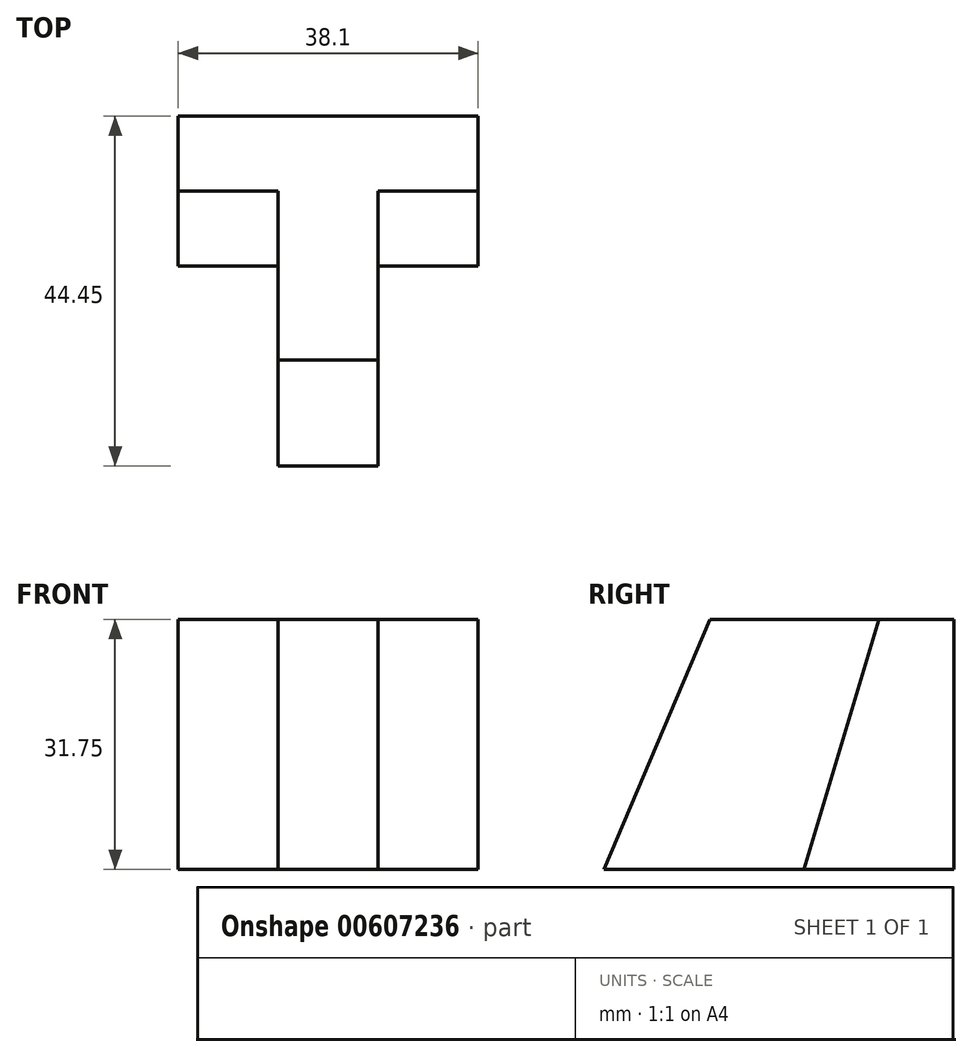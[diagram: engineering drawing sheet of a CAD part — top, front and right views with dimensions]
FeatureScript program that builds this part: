
annotation { "Feature Type Name" : "Feature", "Feature Type Description" : "" }
export const myFeature = defineFeature(function(context is Context, id is Id, definition is map)
    precondition{}
    {
        {
            var Q0;
            Q0=qCreatedBy(makeId("Top.planeOp"),FACE);
            var sketch = newSketch(context, id + "F0", { "sketchPlane" : qUnion([Q0])});
            skLineSegment(sketch, "E0", {"start": v(0, 0) * mm, "end": v(12.7, 0) * mm});
            skLineSegment(sketch, "E1", {"start": v(12.7, 0) * mm, "end": v(12.7, 25.4) * mm});
            skLineSegment(sketch, "E2", {"start": v(12.7, 25.4) * mm, "end": v(25.4, 25.4) * mm});
            skLineSegment(sketch, "E3", {"start": v(25.4, 25.4) * mm, "end": v(25.4, 44.45) * mm});
            skLineSegment(sketch, "E4", {"start": v(25.4, 44.45) * mm, "end": v(-12.7, 44.45) * mm});
            skLineSegment(sketch, "E5", {"start": v(-12.7, 44.45) * mm, "end": v(-12.7, 25.4) * mm});
            skLineSegment(sketch, "E6", {"start": v(-12.7, 25.4) * mm, "end": v(0, 25.4) * mm});
            skLineSegment(sketch, "E7", {"start": v(0, 25.4) * mm, "end": v(0, 0) * mm});
            skSolve(sketch);
        }
        {
            var Q0;
            Q0 = qSketchRegion(id + "F0", true);
            extrude(context, id + "F1", {"entities" : qUnion([Q0]), "oppositeDirection" : true, "depth" : 31.75 * mm, "offsetDistance" : 25.4 * mm});
        }
        {
            var Q0;
            Q0=makeQuery(id+"F1.opExtrude","SWEPT_FACE",FACE,{"disambiguationData":[OSD([sQuery(id+"F0.wireOp",EDGE,"E5")])]});
            var sketch = newSketch(context, id + "F2", { "sketchPlane" : qUnion([Q0])});
            skLineSegment(sketch, "E8", {"start": v(-25.4, -31.75) * mm, "end": v(-34.92, 0) * mm});
            skSolve(sketch);
        }
        {
            var Q0;
            {var subQ0=sQuery(id+"F2.wireOp",EDGE,"E8");Q0=makeQuery(id+"F2.imprint","IMPRINT",FACE,{"disambiguationData":[TD([[makeQuery(id+"F2.imprint","IMPRINT",EDGE,{"derivedFrom":subQ0}),-1.0]])]});}
            extrude(context, id + "F3", {"entities" : qUnion([Q0]), "operationType" : NewBodyOperationType.REMOVE, "oppositeDirection" : true, "depth" : 12.7 * mm, "offsetDistance" : 25.4 * mm});
        }
        {
            var Q0;
            Q0=makeQuery(id+"F3.boolean.opBoolean","MERGE",FACE,{"derivedFrom":[makeQuery(id+"F1.opExtrude","SWEPT_FACE",FACE,{"disambiguationData":[OSD([sQuery(id+"F0.wireOp",EDGE,"E7")])]}),makeQuery(id+"F3.opExtrude","CAP_FACE",FACE,{"disambiguationData":[OSD([sQuery(id+"F0.wireOp",EDGE,"E5"),sQuery(id+"F0.wireOp",EDGE,"E6"),sQuery(id+"F2.wireOp",EDGE,"E8")])],"isStart":false})]});
            var sketch = newSketch(context, id + "F4", { "sketchPlane" : qUnion([Q0])});
            skLineSegment(sketch, "E9", {"start": v(0, -31.75) * mm, "end": v(-13.48, 0) * mm});
            skSolve(sketch);
        }
        {
            var Q0;
            {var subQ0=sQuery(id+"F4.wireOp",EDGE,"E9");Q0=makeQuery(id+"F4.imprint","IMPRINT",FACE,{"disambiguationData":[TD([[makeQuery(id+"F4.imprint","IMPRINT",EDGE,{"derivedFrom":subQ0}),-1.0]])]});}
            extrude(context, id + "F5", {"entities" : qUnion([Q0]), "operationType" : NewBodyOperationType.REMOVE, "oppositeDirection" : true, "depth" : 12.7 * mm, "offsetDistance" : 25.4 * mm});
        }
        {
            var Q0;
            Q0=makeQuery(id+"F1.opExtrude","SWEPT_FACE",FACE,{"disambiguationData":[OSD([sQuery(id+"F0.wireOp",EDGE,"E3")])]});
            var sketch = newSketch(context, id + "F6", { "sketchPlane" : qUnion([Q0])});
            skLineSegment(sketch, "E10", {"start": v(34.92, 0) * mm, "end": v(25.4, -31.75) * mm});
            skSolve(sketch);
        }
        {
            var Q0;
            {var subQ0=sQuery(id+"F6.wireOp",EDGE,"E10");Q0=makeQuery(id+"F6.imprint","IMPRINT",FACE,{"disambiguationData":[TD([[makeQuery(id+"F6.imprint","IMPRINT",EDGE,{"derivedFrom":subQ0}),-1.0]])]});}
            extrude(context, id + "F7", {"entities" : qUnion([Q0]), "operationType" : NewBodyOperationType.REMOVE, "oppositeDirection" : true, "depth" : 12.7 * mm, "offsetDistance" : 25.4 * mm});
        }
    });
